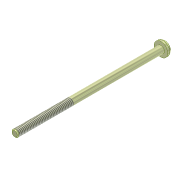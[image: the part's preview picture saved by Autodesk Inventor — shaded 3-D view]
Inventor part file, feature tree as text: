
AUTODESK INVENTOR PART (.ipt)
format: ipt  version: 2013 (Build 170138000, 138)  size: 97,280 bytes
history: native  units: mm
features: imported_body x1, thread x1
ambient origin geometry x8: Origin, YZ Plane, XZ Plane, XY Plane, X Axis, Y Axis, Z Axis, Center Point
bodies: Solid1 (feature_tree)
feature tree (2):
  imported_body  "Base1"
  thread  "Thread1"  [1 undecoded]
note: 1 required parameter value undecoded (feature->parameter linkage not recoverable at this tier; creation-order binding heuristic only, values carry confidence <= 0.55)
